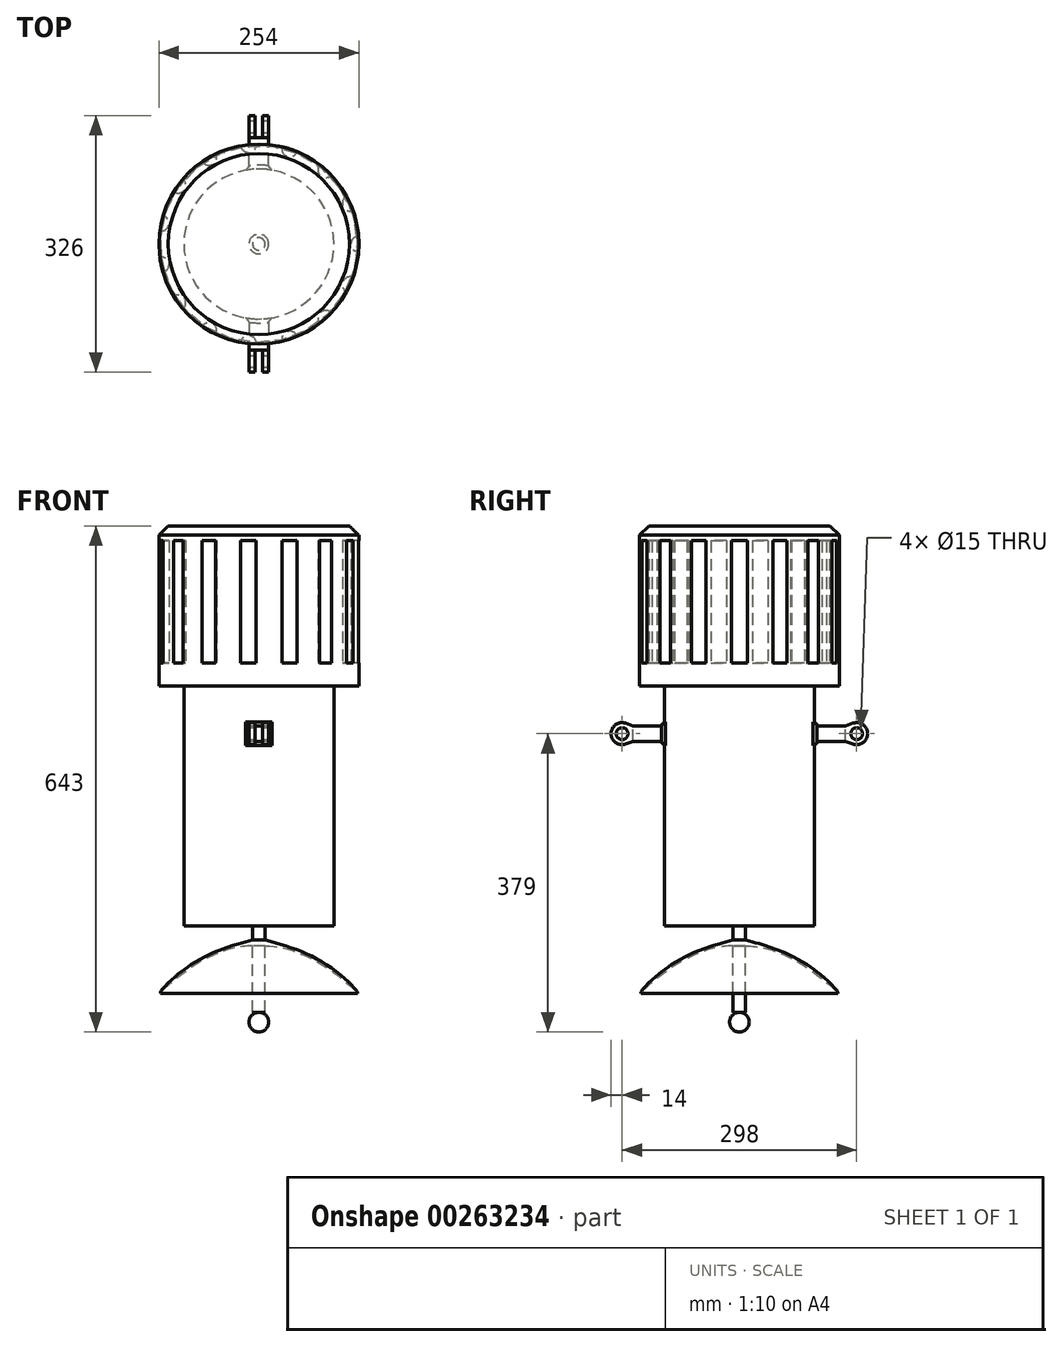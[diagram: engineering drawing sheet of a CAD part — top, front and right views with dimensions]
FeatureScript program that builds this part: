
annotation { "Feature Type Name" : "Feature", "Feature Type Description" : "" }
export const myFeature = defineFeature(function(context is Context, id is Id, definition is map)
    precondition{}
    {
        {
            var Q0;
            Q0=qCreatedBy(makeId("Top.planeOp"),FACE);
            var sketch = newSketch(context, id + "F0", { "sketchPlane" : qUnion([Q0])});
            skCircle(sketch, "E0", {"center": v(0, 0) * mm, "radius": 127 * mm});
            skSolve(sketch);
        }
        {
            var Q0;
            Q0=makeQuery(id+"F0.imprint","IMPRINT",FACE,{"disambiguationData":[TD([[makeQuery(id+"F0.imprint","IMPRINT",EDGE,{"derivedFrom":sQuery(id+"F0.wireOp",EDGE,"E0")}),1.0]])]});
            extrude(context, id + "F1", {"entities" : qUnion([Q0]), "endBound" : BoundingType.SYMMETRIC, "depth" : 508 * mm});
        }
        {
            var Q0;
            Q0=makeQuery(id+"F1.opExtrude","CAP_FACE",FACE,{"disambiguationData":[OSD([sQuery(id+"F0.wireOp",EDGE,"E0")])],"isStart":true});
            var sketch = newSketch(context, id + "F2", { "sketchPlane" : qUnion([Q0])});
            skCircle(sketch, "E1", {"center": v(0, 0) * mm, "radius": 95.25 * mm});
            skSolve(sketch);
        }
        {
            var Q0;
            Q0=makeQuery(id+"F2.imprint","IMPRINT",FACE,{"disambiguationData":[TD([[makeQuery(id+"F2.imprint","IMPRINT",EDGE,{"derivedFrom":sQuery(id+"F2.wireOp",EDGE,"E1")}),-1.0]])]});
            extrude(context, id + "F3", {"entities" : qUnion([Q0]), "operationType" : NewBodyOperationType.REMOVE, "oppositeDirection" : true, "depth" : 304.8 * mm});
        }
        {
            var Q0;
            Q0=qCreatedBy(makeId("Front.planeOp"),FACE);
            var sketch = newSketch(context, id + "F4", { "sketchPlane" : qUnion([Q0])});
            skLineSegment(sketch, "E2.0.0", {"start": v(95.25, -254) * mm, "end": v(-95.25, -254) * mm});
            skLineSegment(sketch, "E3", {"start": v(0, -254) * mm, "end": v(0, -279) * mm});
            skLineSegment(sketch, "E4", {"start": v(0, -254) * mm, "end": v(8, -254) * mm});
            skLineSegment(sketch, "E5", {"start": v(8, -254) * mm, "end": v(8, -272) * mm});
            skFitSpline(sketch, "E6", {"points": [v(8, -272) * mm, v(82.52, -301.2) * mm, v(124.73, -337.73) * mm, v(125.08, -340.21) * mm], "startDerivative": vector(152.34, -42.53) * mm, "endDerivative": vector(-4.33, -21.8) * mm});
            skFitSpline(sketch, "E7", {"points": [v(0, -279) * mm, v(37.2, -283.84) * mm, v(90.27, -309.98) * mm, v(123.63, -337.73) * mm, v(124.73, -339.57) * mm, v(125.08, -340.21) * mm], "startDerivative": vector(133.4, -6.9) * mm, "endDerivative": vector(9.64, -16.09) * mm});
            skSolve(sketch);
        }
        {
            var Q0;
            Q0 = qSketchRegion(id + "F4", true);
            var Q1;
            Q1=sQuery(id+"F4.wireOp",EDGE,"E3");
            revolve(context, id + "F5", {"operationType" : NewBodyOperationType.ADD, "entities" : qUnion([Q0]), "axis" : qUnion([Q1]), "revolveType" : RevolveType.FULL});
        }
        {
            var Q0;
            Q0=makeQuery(id+"F1.opExtrude","CAP_FACE",FACE,{"disambiguationData":[OSD([sQuery(id+"F0.wireOp",EDGE,"E0")])],"isStart":true});
            var sketch = newSketch(context, id + "F6", { "sketchPlane" : qUnion([Q0])});
            skCircle(sketch, "E8", {"center": v(0, 0) * mm, "radius": 8 * mm});
            skSolve(sketch);
        }
        {
            var Q0;
            Q0 = qSketchRegion(id + "F6", true);
            extrude(context, id + "F7", {"entities" : qUnion([Q0]), "operationType" : NewBodyOperationType.ADD, "depth" : 110 * mm});
        }
        {
            var Q0;
            Q0=qCreatedBy(makeId("Front.planeOp"),FACE);
            var sketch = newSketch(context, id + "F8", { "sketchPlane" : qUnion([Q0])});
            skLineSegment(sketch, "E9.0.0", {"start": v(8, -364) * mm, "end": v(-8, -364) * mm});
            skLineSegment(sketch, "E10", {"start": v(0, -364) * mm, "end": v(0, -389) * mm});
            skPoint(sketch, "E10.endSnap0", {"position": v(0, -364) * mm});
            skArc(sketch, "E11", {"start": v(0, -364) * mm, "mid": v(-12.5, -376.5) * mm, "end": v(0, -389) * mm});
            skSolve(sketch);
        }
        {
            var Q0;
            Q0=makeQuery(id+"F8.imprint","IMPRINT",FACE,{"disambiguationData":[TD([[makeQuery(id+"F8.imprint","IMPRINT",EDGE,{"derivedFrom":sQuery(id+"F8.wireOp",EDGE,"E10")}),-1.0]])]});
            var Q1;
            Q1=sQuery(id+"F8.wireOp",EDGE,"E10");
            revolve(context, id + "F9", {"operationType" : NewBodyOperationType.ADD, "entities" : qUnion([Q0]), "axis" : qUnion([Q1]), "revolveType" : RevolveType.FULL});
        }
        {
            var Q0;
            Q0=makeQuery(id+"F3.boolean.opBoolean","COPY",EDGE,{"derivedFrom":makeQuery(id+"F3.opExtrude","CAP_EDGE",EDGE,{"disambiguationData":[OSD([sQuery(id+"F2.wireOp",EDGE,"E1")])],"isStart":true})});
            var Q1;
            Q1=makeQuery(id+"F1.opExtrude","CAP_EDGE",EDGE,{"disambiguationData":[OSD([sQuery(id+"F0.wireOp",EDGE,"E0")])],"isStart":false});
            var Q2;
            Q2=makeQuery(id+"F3.boolean.opBoolean","COPY",EDGE,{"derivedFrom":makeQuery(id+"F3.opExtrude","CAP_EDGE",EDGE,{"disambiguationData":[OSD([sQuery(id+"F0.wireOp",EDGE,"E0")])],"isStart":false})});
            chamfer(context, id + "F10", {"entities" : qUnion([Q0, Q1, Q2]), "width" : 12 * mm, "tangentPropagation" : true});
        }
        {
            var Q0;
            Q0=qCreatedBy(makeId("Top.planeOp"),FACE);
            cPlane(context, id + "F11", {"entities" : qUnion([Q0]), "cplaneType" : CPlaneType.OFFSET, "offset" : 80 * mm, "width" : 150 * mm, "height" : 150 * mm});
        }
        {
            var Q0;
            Q0=qCreatedBy(id+"F11.planeOp",FACE);
            var sketch = newSketch(context, id + "F12", { "sketchPlane" : qUnion([Q0])});
            skArc(sketch, "E12.0", {"start": v(119.72, 42.37) * mm, "mid": v(116.02, 51.66) * mm, "end": v(111.6, 60.62) * mm});
            skLineSegment(sketch, "E13", {"start": v(0, 0) * mm, "end": v(182.8, 0) * mm, "construction": true});
            skArc(sketch, "E14", {"start": v(126.6, 10) * mm, "mid": v(117, 0) * mm, "end": v(126.6, -10) * mm});
            skArc(sketch, "E15.1.0", {"start": v(111.6, 60.62) * mm, "mid": v(106.88, 47.59) * mm, "end": v(119.72, 42.37) * mm});
            skArc(sketch, "E15.2.0", {"start": v(77.3, 100.77) * mm, "mid": v(78.29, 86.95) * mm, "end": v(92.14, 87.4) * mm});
            skArc(sketch, "E15.3.0", {"start": v(29.62, 123.5) * mm, "mid": v(36.15, 111.27) * mm, "end": v(48.63, 117.32) * mm});
            skArc(sketch, "E15.4.0", {"start": v(-23.17, 124.87) * mm, "mid": v(-12.23, 116.36) * mm, "end": v(-3.3, 126.96) * mm});
            skArc(sketch, "E15.5.0", {"start": v(-71.96, 104.65) * mm, "mid": v(-58.5, 101.32) * mm, "end": v(-54.65, 114.64) * mm});
            skArc(sketch, "E15.6.0", {"start": v(-108.3, 66.33) * mm, "mid": v(-94.65, 68.77) * mm, "end": v(-96.55, 82.5) * mm});
            skArc(sketch, "E15.7.0", {"start": v(-125.92, 16.55) * mm, "mid": v(-114.44, 24.33) * mm, "end": v(-121.76, 36.1) * mm});
            skArc(sketch, "E15.8.0", {"start": v(-121.76, -36.1) * mm, "mid": v(-114.44, -24.33) * mm, "end": v(-125.92, -16.55) * mm});
            skArc(sketch, "E15.9.0", {"start": v(-96.55, -82.5) * mm, "mid": v(-94.65, -68.77) * mm, "end": v(-108.3, -66.33) * mm});
            skArc(sketch, "E15.10.0", {"start": v(-54.65, -114.64) * mm, "mid": v(-58.5, -101.32) * mm, "end": v(-71.96, -104.65) * mm});
            skArc(sketch, "E15.11.0", {"start": v(-3.3, -126.96) * mm, "mid": v(-12.23, -116.36) * mm, "end": v(-23.17, -124.87) * mm});
            skArc(sketch, "E15.12.0", {"start": v(48.63, -117.32) * mm, "mid": v(36.15, -111.27) * mm, "end": v(29.62, -123.5) * mm});
            skArc(sketch, "E15.13.0", {"start": v(92.14, -87.4) * mm, "mid": v(78.29, -86.95) * mm, "end": v(77.3, -100.77) * mm});
            skArc(sketch, "E15.14.0", {"start": v(119.72, -42.37) * mm, "mid": v(106.88, -47.59) * mm, "end": v(111.6, -60.62) * mm});
            skArc(sketch, "E16.trimOffspring", {"start": v(126.6, -10) * mm, "mid": v(127, 0) * mm, "end": v(126.6, 10) * mm});
            skArc(sketch, "E17.trimOffspring", {"start": v(111.6, -60.62) * mm, "mid": v(116.02, -51.66) * mm, "end": v(119.72, -42.37) * mm});
            skArc(sketch, "E18.trimOffspring", {"start": v(77.3, -100.77) * mm, "mid": v(84.98, -94.38) * mm, "end": v(92.14, -87.4) * mm});
            skArc(sketch, "E19.trimOffspring", {"start": v(92.14, 87.4) * mm, "mid": v(84.98, 94.38) * mm, "end": v(77.3, 100.77) * mm});
            skArc(sketch, "E20.trimOffspring", {"start": v(48.63, 117.32) * mm, "mid": v(39.25, 120.78) * mm, "end": v(29.62, 123.5) * mm});
            skArc(sketch, "E21.trimOffspring", {"start": v(-3.3, 126.96) * mm, "mid": v(-13.28, 126.3) * mm, "end": v(-23.17, 124.87) * mm});
            skArc(sketch, "E22.trimOffspring", {"start": v(-54.65, 114.64) * mm, "mid": v(-63.5, 109.99) * mm, "end": v(-71.96, 104.65) * mm});
            skArc(sketch, "E23.trimOffspring", {"start": v(-96.55, 82.5) * mm, "mid": v(-102.75, 74.65) * mm, "end": v(-108.3, 66.33) * mm});
            skArc(sketch, "E24.trimOffspring", {"start": v(-121.76, 36.1) * mm, "mid": v(-124.22, 26.4) * mm, "end": v(-125.92, 16.55) * mm});
            skArc(sketch, "E25.trimOffspring", {"start": v(-125.92, -16.55) * mm, "mid": v(-124.22, -26.4) * mm, "end": v(-121.76, -36.1) * mm});
            skArc(sketch, "E26.trimOffspring", {"start": v(-108.3, -66.33) * mm, "mid": v(-102.75, -74.65) * mm, "end": v(-96.55, -82.5) * mm});
            skArc(sketch, "E27.trimOffspring", {"start": v(-71.96, -104.65) * mm, "mid": v(-63.5, -109.99) * mm, "end": v(-54.65, -114.64) * mm});
            skArc(sketch, "E28.trimOffspring", {"start": v(-23.17, -124.87) * mm, "mid": v(-13.28, -126.3) * mm, "end": v(-3.3, -126.96) * mm});
            skArc(sketch, "E29.trimOffspring", {"start": v(29.62, -123.5) * mm, "mid": v(39.25, -120.78) * mm, "end": v(48.63, -117.32) * mm});
            skSolve(sketch);
        }
        {
            var Q0;
            Q0 = qSketchRegion(id + "F12", true);
            extrude(context, id + "F13", {"entities" : qUnion([Q0]), "operationType" : NewBodyOperationType.REMOVE, "depth" : 155 * mm});
        }
        {
            var Q0;
            Q0=qCreatedBy(makeId("Top.planeOp"),FACE);
            var sketch = newSketch(context, id + "F14", { "sketchPlane" : qUnion([Q0])});
            skArc(sketch, "E30", {"start": v(12.5, 94.17) * mm, "mid": v(0, 95) * mm, "end": v(-12.5, 94.17) * mm});
            skPoint(sketch, "E31", {"position": v(12.5, 0) * mm});
            skPoint(sketch, "E32", {"position": v(-12.5, 0) * mm});
            skLineSegment(sketch, "E33", {"start": v(12.5, 94.17) * mm, "end": v(12.5, 135) * mm});
            skLineSegment(sketch, "E34", {"start": v(-12.5, 94.17) * mm, "end": v(-12.5, 135) * mm});
            skLineSegment(sketch, "E35", {"start": v(-12.5, -94.17) * mm, "end": v(-12.5, -135) * mm});
            skLineSegment(sketch, "E36", {"start": v(12.5, -94.17) * mm, "end": v(12.5, -135) * mm});
            skLineSegment(sketch, "E37", {"start": v(12.5, 135) * mm, "end": v(-12.5, 135) * mm});
            skLineSegment(sketch, "E38", {"start": v(12.5, -135) * mm, "end": v(-12.5, -135) * mm});
            skArc(sketch, "E39.trimOffspring", {"start": v(-12.5, -94.17) * mm, "mid": v(0, -95) * mm, "end": v(12.5, -94.17) * mm});
            skSolve(sketch);
        }
        {
            var Q0;
            Q0 = qSketchRegion(id + "F14", true);
            extrude(context, id + "F15", {"entities" : qUnion([Q0]), "operationType" : NewBodyOperationType.ADD, "oppositeDirection" : true, "depth" : 20 * mm});
        }
        {
            var Q0;
            Q0=makeQuery(id+"F15.opExtrude","SWEPT_FACE",FACE,{"disambiguationData":[OSD([sQuery(id+"F14.wireOp",EDGE,"E35")])]});
            var sketch = newSketch(context, id + "F16", { "sketchPlane" : qUnion([Q0])});
            skLineSegment(sketch, "E40", {"start": v(0, 0) * mm, "end": v(0, -51.85) * mm, "construction": true});
            skLineSegment(sketch, "E41", {"start": v(135, -10) * mm, "end": v(149, -10) * mm, "construction": true});
            skArc(sketch, "E42", {"start": v(144.46, -23.24) * mm, "mid": v(163, -10) * mm, "end": v(144.46, 3.24) * mm});
            skLineSegment(sketch, "E43", {"start": v(135, -20) * mm, "end": v(144.46, -23.24) * mm});
            skLineSegment(sketch, "E44", {"start": v(135, 0) * mm, "end": v(144.46, 3.24) * mm});
            skLineSegment(sketch, "E45.MirrorCS", {"start": v(-135, -20) * mm, "end": v(-144.46, -23.24) * mm});
            skArc(sketch, "E46.MirrorCS", {"start": v(-144.46, -23.24) * mm, "mid": v(-163, -10) * mm, "end": v(-144.46, 3.24) * mm});
            skLineSegment(sketch, "E47.MirrorCS", {"start": v(-135, 0) * mm, "end": v(-144.46, 3.24) * mm});
            skLineSegment(sketch, "E48", {"start": v(135, -20) * mm, "end": v(135, 0) * mm});
            skLineSegment(sketch, "E49", {"start": v(-135, -20) * mm, "end": v(-135, 0) * mm});
            skSolve(sketch);
        }
        {
            var Q0;
            Q0 = qSketchRegion(id + "F16", true);
            var Q1;
            Q1=makeQuery(id+"F15.opExtrude","SWEPT_FACE",FACE,{"disambiguationData":[OSD([sQuery(id+"F14.wireOp",EDGE,"E36")])]});
            extrude(context, id + "F17", {"entities" : qUnion([Q0]), "operationType" : NewBodyOperationType.ADD, "endBound" : BoundingType.UP_TO_SURFACE, "oppositeDirection" : true, "endBoundEntityFace" : qUnion([Q1]), "depth" : 25 * mm});
        }
        {
            var Q0;
            Q0=makeQuery(id+"F15.boolean.opBoolean","INTERSECT",EDGE,{"derivedFrom":[makeQuery(id+"F3.boolean.opBoolean","COPY",FACE,{"derivedFrom":makeQuery(id+"F3.opExtrude","SWEPT_FACE",FACE,{"disambiguationData":[OSD([sQuery(id+"F2.wireOp",EDGE,"E1")])]})}),makeQuery(id+"F15.opExtrude","CAP_FACE",FACE,{"disambiguationData":[OSD([sQuery(id+"F14.wireOp",EDGE,"E35"),sQuery(id+"F14.wireOp",EDGE,"E36"),sQuery(id+"F14.wireOp",EDGE,"E38"),sQuery(id+"F14.wireOp",EDGE,"E39.trimOffspring")])],"isStart":false})]});
            var Q1;
            Q1=makeQuery(id+"F15.boolean.opBoolean","INTERSECT",EDGE,{"derivedFrom":[makeQuery(id+"F3.boolean.opBoolean","COPY",FACE,{"derivedFrom":makeQuery(id+"F3.opExtrude","SWEPT_FACE",FACE,{"disambiguationData":[OSD([sQuery(id+"F2.wireOp",EDGE,"E1")])]})}),makeQuery(id+"F15.opExtrude","SWEPT_FACE",FACE,{"disambiguationData":[OSD([sQuery(id+"F14.wireOp",EDGE,"E35")])]})]});
            var Q2;
            Q2=makeQuery(id+"F15.boolean.opBoolean","INTERSECT",EDGE,{"derivedFrom":[makeQuery(id+"F3.boolean.opBoolean","COPY",FACE,{"derivedFrom":makeQuery(id+"F3.opExtrude","SWEPT_FACE",FACE,{"disambiguationData":[OSD([sQuery(id+"F2.wireOp",EDGE,"E1")])]})}),makeQuery(id+"F15.opExtrude","SWEPT_FACE",FACE,{"disambiguationData":[OSD([sQuery(id+"F14.wireOp",EDGE,"E36")])]})]});
            var Q3;
            Q3=makeQuery(id+"F15.boolean.opBoolean","INTERSECT",EDGE,{"derivedFrom":[makeQuery(id+"F3.boolean.opBoolean","COPY",FACE,{"derivedFrom":makeQuery(id+"F3.opExtrude","SWEPT_FACE",FACE,{"disambiguationData":[OSD([sQuery(id+"F2.wireOp",EDGE,"E1")])]})}),makeQuery(id+"F15.opExtrude","CAP_FACE",FACE,{"disambiguationData":[OSD([sQuery(id+"F14.wireOp",EDGE,"E35"),sQuery(id+"F14.wireOp",EDGE,"E36"),sQuery(id+"F14.wireOp",EDGE,"E38"),sQuery(id+"F14.wireOp",EDGE,"E39.trimOffspring")])],"isStart":true})]});
            var Q4;
            Q4=makeQuery(id+"F15.boolean.opBoolean","INTERSECT",EDGE,{"derivedFrom":[makeQuery(id+"F3.boolean.opBoolean","COPY",FACE,{"derivedFrom":makeQuery(id+"F3.opExtrude","SWEPT_FACE",FACE,{"disambiguationData":[OSD([sQuery(id+"F2.wireOp",EDGE,"E1")])]})}),makeQuery(id+"F15.opExtrude","CAP_FACE",FACE,{"disambiguationData":[OSD([sQuery(id+"F14.wireOp",EDGE,"E30"),sQuery(id+"F14.wireOp",EDGE,"E33"),sQuery(id+"F14.wireOp",EDGE,"E34"),sQuery(id+"F14.wireOp",EDGE,"E37")])],"isStart":false})]});
            var Q5;
            Q5=makeQuery(id+"F15.boolean.opBoolean","INTERSECT",EDGE,{"derivedFrom":[makeQuery(id+"F3.boolean.opBoolean","COPY",FACE,{"derivedFrom":makeQuery(id+"F3.opExtrude","SWEPT_FACE",FACE,{"disambiguationData":[OSD([sQuery(id+"F2.wireOp",EDGE,"E1")])]})}),makeQuery(id+"F15.opExtrude","SWEPT_FACE",FACE,{"disambiguationData":[OSD([sQuery(id+"F14.wireOp",EDGE,"E34")])]})]});
            var Q6;
            Q6=makeQuery(id+"F15.boolean.opBoolean","INTERSECT",EDGE,{"derivedFrom":[makeQuery(id+"F3.boolean.opBoolean","COPY",FACE,{"derivedFrom":makeQuery(id+"F3.opExtrude","SWEPT_FACE",FACE,{"disambiguationData":[OSD([sQuery(id+"F2.wireOp",EDGE,"E1")])]})}),makeQuery(id+"F15.opExtrude","CAP_FACE",FACE,{"disambiguationData":[OSD([sQuery(id+"F14.wireOp",EDGE,"E30"),sQuery(id+"F14.wireOp",EDGE,"E33"),sQuery(id+"F14.wireOp",EDGE,"E34"),sQuery(id+"F14.wireOp",EDGE,"E37")])],"isStart":true})]});
            var Q7;
            Q7=makeQuery(id+"F15.boolean.opBoolean","INTERSECT",EDGE,{"derivedFrom":[makeQuery(id+"F3.boolean.opBoolean","COPY",FACE,{"derivedFrom":makeQuery(id+"F3.opExtrude","SWEPT_FACE",FACE,{"disambiguationData":[OSD([sQuery(id+"F2.wireOp",EDGE,"E1")])]})}),makeQuery(id+"F15.opExtrude","SWEPT_FACE",FACE,{"disambiguationData":[OSD([sQuery(id+"F14.wireOp",EDGE,"E33")])]})]});
            chamfer(context, id + "F18", {"entities" : qUnion([Q0, Q1, Q2, Q3, Q4, Q5, Q6, Q7]), "width" : 5 * mm, "tangentPropagation" : true});
        }
        {
            var Q0;
            Q0=makeQuery(id+"F17.boolean.opBoolean","MERGE",FACE,{"derivedFrom":[makeQuery(id+"F15.opExtrude","SWEPT_FACE",FACE,{"disambiguationData":[OSD([sQuery(id+"F14.wireOp",EDGE,"E33")])]}),makeQuery(id+"F17.opExtrude","CAP_FACE",FACE,{"disambiguationData":[OSD([sQuery(id+"F14.wireOp",EDGE,"E36")]),ownerDisambiguation([makeQuery(id+"F17.opExtrude","SWEPT_BODY",BODY,{"disambiguationData":[OSD([sQuery(id+"F16.wireOp",EDGE,"E45.MirrorCS"),sQuery(id+"F16.wireOp",EDGE,"E46.MirrorCS"),sQuery(id+"F16.wireOp",EDGE,"E47.MirrorCS"),sQuery(id+"F16.wireOp",EDGE,"E49")])]})])],"isStart":false})]});
            var sketch = newSketch(context, id + "F19", { "sketchPlane" : qUnion([Q0])});
            skCircle(sketch, "E50", {"center": v(149, -10) * mm, "radius": 7.5 * mm});
            skLineSegment(sketch, "E51", {"start": v(0, 0) * mm, "end": v(0, -54.57) * mm, "construction": true});
            skCircle(sketch, "E52.MirrorC", {"center": v(-149, -10) * mm, "radius": 7.5 * mm});
            skSolve(sketch);
        }
        {
            var Q0;
            Q0 = qSketchRegion(id + "F19", true);
            extrude(context, id + "F20", {"entities" : qUnion([Q0]), "operationType" : NewBodyOperationType.REMOVE, "oppositeDirection" : true, "depth" : 25 * mm});
        }
        {
            var Q0;
            Q0=makeQuery(id+"F17.boolean.opBoolean","MERGE",FACE,{"derivedFrom":[makeQuery(id+"F15.opExtrude","SWEPT_FACE",FACE,{"disambiguationData":[OSD([sQuery(id+"F14.wireOp",EDGE,"E33")])]}),makeQuery(id+"F17.opExtrude","CAP_FACE",FACE,{"disambiguationData":[OSD([sQuery(id+"F14.wireOp",EDGE,"E36")]),ownerDisambiguation([makeQuery(id+"F17.opExtrude","SWEPT_BODY",BODY,{"disambiguationData":[OSD([sQuery(id+"F16.wireOp",EDGE,"E45.MirrorCS"),sQuery(id+"F16.wireOp",EDGE,"E46.MirrorCS"),sQuery(id+"F16.wireOp",EDGE,"E47.MirrorCS"),sQuery(id+"F16.wireOp",EDGE,"E49")])]})])],"isStart":false})]});
            var Q1;
            Q1=makeQuery(id+"F17.boolean.opBoolean","MERGE",FACE,{"derivedFrom":[makeQuery(id+"F15.opExtrude","SWEPT_FACE",FACE,{"disambiguationData":[OSD([sQuery(id+"F14.wireOp",EDGE,"E34")])]}),makeQuery(id+"F17.opExtrude","CAP_FACE",FACE,{"disambiguationData":[OSD([sQuery(id+"F16.wireOp",EDGE,"E45.MirrorCS"),sQuery(id+"F16.wireOp",EDGE,"E46.MirrorCS"),sQuery(id+"F16.wireOp",EDGE,"E47.MirrorCS"),sQuery(id+"F16.wireOp",EDGE,"E49")])],"isStart":true})]});
            cPlane(context, id + "F21", {"entities" : qUnion([Q0, Q1]), "cplaneType" : CPlaneType.MID_PLANE, "offset" : 25 * mm, "width" : 150 * mm, "height" : 150 * mm});
        }
        {
            var Q0;
            Q0=qCreatedBy(id+"F21.planeOp",FACE);
            var sketch = newSketch(context, id + "F22", { "sketchPlane" : qUnion([Q0])});
            skArc(sketch, "E53.0", {"start": v(144.46, 3.24) * mm, "mid": v(163, -10) * mm, "end": v(144.46, -23.24) * mm});
            skLineSegment(sketch, "E54.0", {"start": v(144.46, 3.24) * mm, "end": v(135, 0) * mm});
            skLineSegment(sketch, "E55.0", {"start": v(144.46, -23.24) * mm, "end": v(135, -20) * mm});
            skLineSegment(sketch, "E56", {"start": v(135, -20) * mm, "end": v(135, 0) * mm});
            skLineSegment(sketch, "E57", {"start": v(0, 0) * mm, "end": v(0, -55) * mm, "construction": true});
            skLineSegment(sketch, "E58.MirrorCS", {"start": v(-135, -20) * mm, "end": v(-135, 0) * mm});
            skLineSegment(sketch, "E59.MirrorCS", {"start": v(-144.46, 3.24) * mm, "end": v(-135, 0) * mm});
            skArc(sketch, "E60.MirrorCS", {"start": v(-144.46, 3.24) * mm, "mid": v(-163, -10) * mm, "end": v(-144.46, -23.24) * mm});
            skLineSegment(sketch, "E61.MirrorCS", {"start": v(-144.46, -23.24) * mm, "end": v(-135, -20) * mm});
            skSolve(sketch);
        }
        {
            var Q0;
            Q0 = qSketchRegion(id + "F22", true);
            extrude(context, id + "F23", {"entities" : qUnion([Q0]), "operationType" : NewBodyOperationType.REMOVE, "endBound" : BoundingType.SYMMETRIC, "oppositeDirection" : true, "depth" : 10 * mm});
        }
    });
